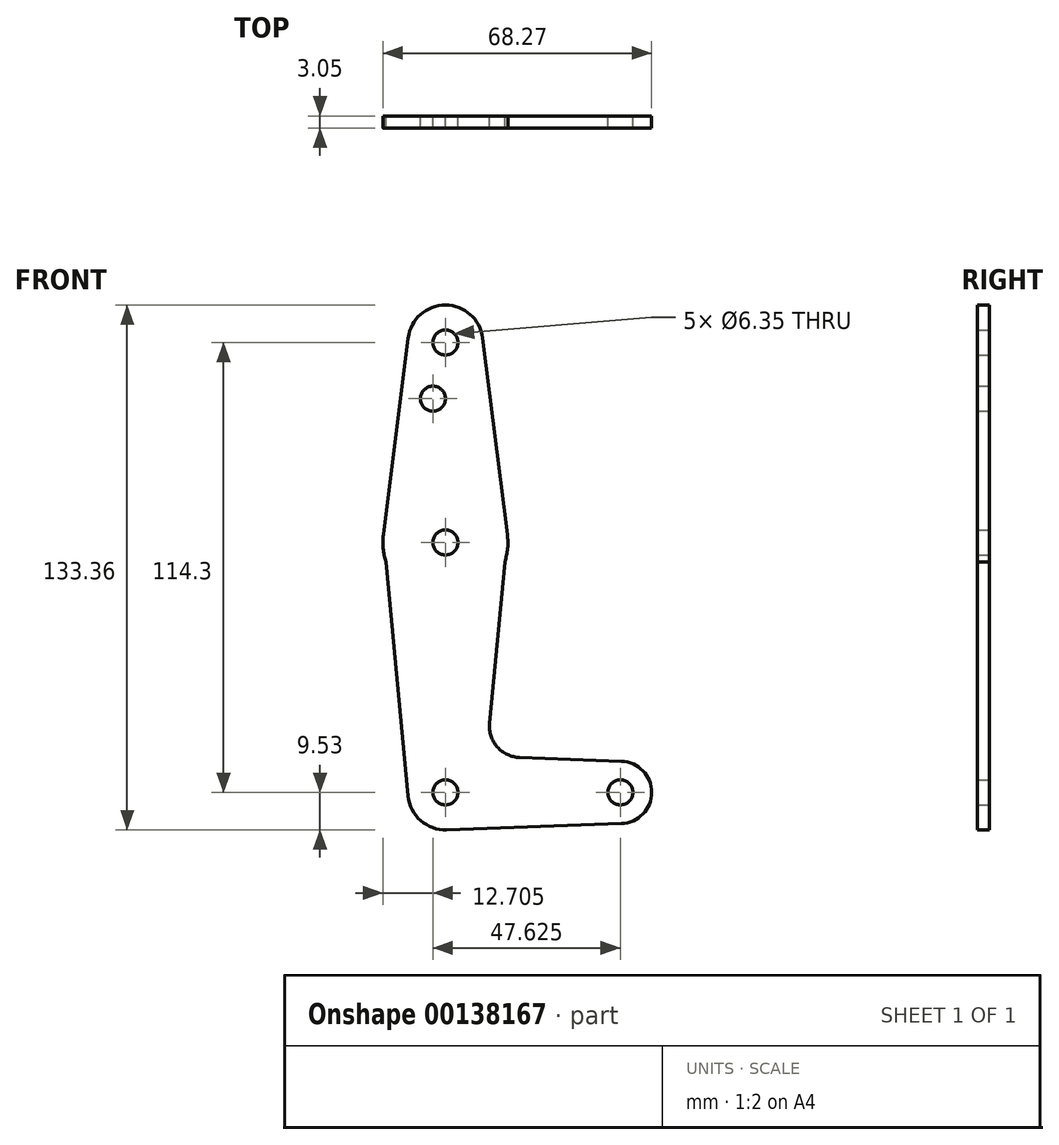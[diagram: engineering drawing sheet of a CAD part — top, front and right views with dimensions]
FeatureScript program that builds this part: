
annotation { "Feature Type Name" : "Feature", "Feature Type Description" : "" }
export const myFeature = defineFeature(function(context is Context, id is Id, definition is map)
    precondition{}
    {
        {
            var Q0;
            Q0=qCreatedBy(makeId("Front.planeOp"),FACE);
            var sketch = newSketch(context, id + "F0", { "sketchPlane" : qUnion([Q0])});
            skLineSegment(sketch, "E0", {"start": v(0, 0) * mm, "end": v(0, 114.3) * mm});
            skLineSegment(sketch, "E1", {"start": v(0, 0) * mm, "end": v(44.45, 0) * mm});
            skCircle(sketch, "E2", {"center": v(0, 0) * mm, "radius": 9.53 * mm});
            skCircle(sketch, "E3", {"center": v(0, 114.3) * mm, "radius": 9.53 * mm});
            skCircle(sketch, "E4", {"center": v(0, 63.5) * mm, "radius": 15.88 * mm});
            skCircle(sketch, "E5", {"center": v(44.45, 0) * mm, "radius": 7.94 * mm});
            skLineSegment(sketch, "E6", {"start": v(-9.45, 115.5) * mm, "end": v(-15.75, 65.48) * mm});
            skLineSegment(sketch, "E7", {"start": v(-15.75, 65.48) * mm, "end": v(-9.48, -0.9) * mm});
            skLineSegment(sketch, "E8", {"start": v(9.45, 115.5) * mm, "end": v(15.75, 65.48) * mm});
            skLineSegment(sketch, "E9", {"start": v(15.75, 65.48) * mm, "end": v(11.22, 17.55) * mm});
            skCircle(sketch, "E10", {"center": v(0, 114.3) * mm, "radius": 3.18 * mm});
            skCircle(sketch, "E11", {"center": v(0, 63.5) * mm, "radius": 3.18 * mm});
            skCircle(sketch, "E12", {"center": v(0, 0) * mm, "radius": 3.18 * mm});
            skCircle(sketch, "E13", {"center": v(44.45, 0) * mm, "radius": 3.18 * mm});
            skCircle(sketch, "E14", {"center": v(-3.18, 100.03) * mm, "radius": 3.18 * mm});
            skLineSegment(sketch, "E15", {"start": v(44.73, 7.93) * mm, "end": v(18.86, 8.86) * mm});
            skLineSegment(sketch, "E16", {"start": v(44.73, -7.93) * mm, "end": v(0, -9.53) * mm});
            skPoint(sketch, "E17.newPointB", {"position": v(0, 9.53) * mm});
            skArc(sketch, "E17.filletArc", {"start": v(11.22, 17.55) * mm, "mid": v(13.16, 11.56) * mm, "end": v(18.86, 8.86) * mm});
            skSolve(sketch);
        }
        {
            var Q0;
            Q0 = qSketchRegion(id + "F0", true);
            var Q1;
            {var subQ0=sQuery(id+"F0.wireOp",EDGE,"E12");var subQ1=sQuery(id+"F0.wireOp",EDGE,"E0");var subQ2=makeQuery(id+"F0.imprint","INTERSECT",VERTEX,{"derivedFrom":[subQ1,subQ0]});Q1=makeQuery(id+"F0.imprint","IMPRINT",FACE,{"disambiguationData":[TD([[makeQuery(id+"F0.imprint","IMPRINT",EDGE,{"disambiguationData":[TD([[subQ2,-1.0]])],"derivedFrom":subQ1}),-1.0]])]});}
            extrude(context, id + "F1", {"entities" : qUnion([Q0, Q1]), "depth" : 3.05 * mm});
        }
    });
